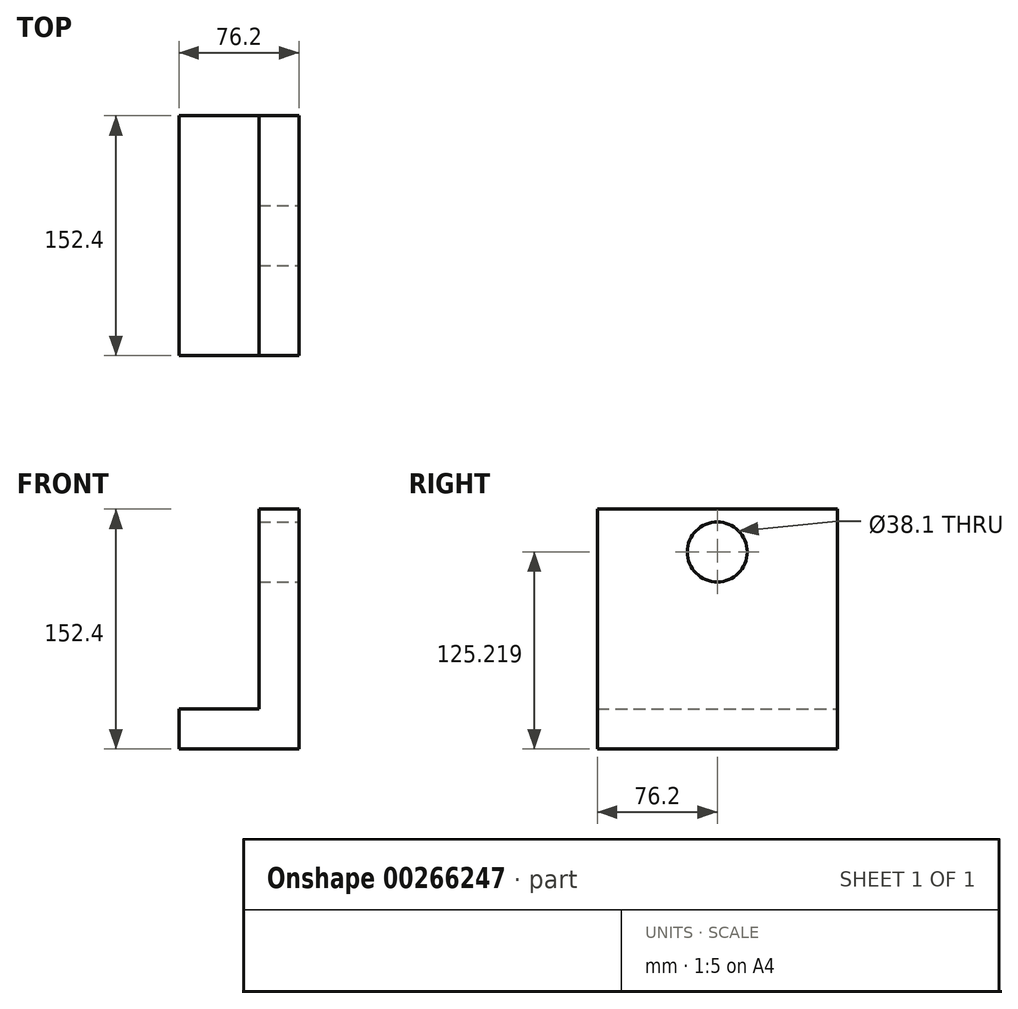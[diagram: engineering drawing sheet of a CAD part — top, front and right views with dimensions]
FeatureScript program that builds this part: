
annotation { "Feature Type Name" : "Feature", "Feature Type Description" : "" }
export const myFeature = defineFeature(function(context is Context, id is Id, definition is map)
    precondition{}
    {
        {
            var Q0;
            Q0=qCreatedBy(makeId("Front.planeOp"),FACE);
            var sketch = newSketch(context, id + "F0", { "sketchPlane" : qUnion([Q0])});
            skLineSegment(sketch, "E0", {"start": v(0, 0) * mm, "end": v(0, 152.4) * mm});
            skLineSegment(sketch, "E1", {"start": v(0, 152.4) * mm, "end": v(-25.4, 152.4) * mm});
            skLineSegment(sketch, "E2", {"start": v(-25.4, 152.4) * mm, "end": v(-25.4, 25.4) * mm});
            skLineSegment(sketch, "E3", {"start": v(-25.4, 25.4) * mm, "end": v(-76.2, 25.4) * mm});
            skLineSegment(sketch, "E4", {"start": v(-76.2, 25.4) * mm, "end": v(-76.2, 0) * mm});
            skLineSegment(sketch, "E5", {"start": v(-76.2, 0) * mm, "end": v(0, 0) * mm});
            skSolve(sketch);
        }
        {
            var Q0;
            Q0 = qSketchRegion(id + "F0", true);
            extrude(context, id + "F1", {"entities" : qUnion([Q0]), "endBound" : BoundingType.SYMMETRIC, "depth" : 152.4 * mm});
        }
        {
            var Q0;
            Q0=makeQuery(id+"F1.opExtrude","SWEPT_FACE",FACE,{"disambiguationData":[OSD([sQuery(id+"F0.wireOp",EDGE,"E0")])]});
            var sketch = newSketch(context, id + "F2", { "sketchPlane" : qUnion([Q0])});
            skCircle(sketch, "E6", {"center": v(0, 125.22) * mm, "radius": 19.05 * mm});
            skSolve(sketch);
        }
        {
            var Q0;
            Q0 = qSketchRegion(id + "F2", true);
            extrude(context, id + "F3", {"entities" : qUnion([Q0]), "operationType" : NewBodyOperationType.REMOVE, "endBound" : BoundingType.THROUGH_ALL, "oppositeDirection" : true, "depth" : 2514.6 * mm});
        }
    });
